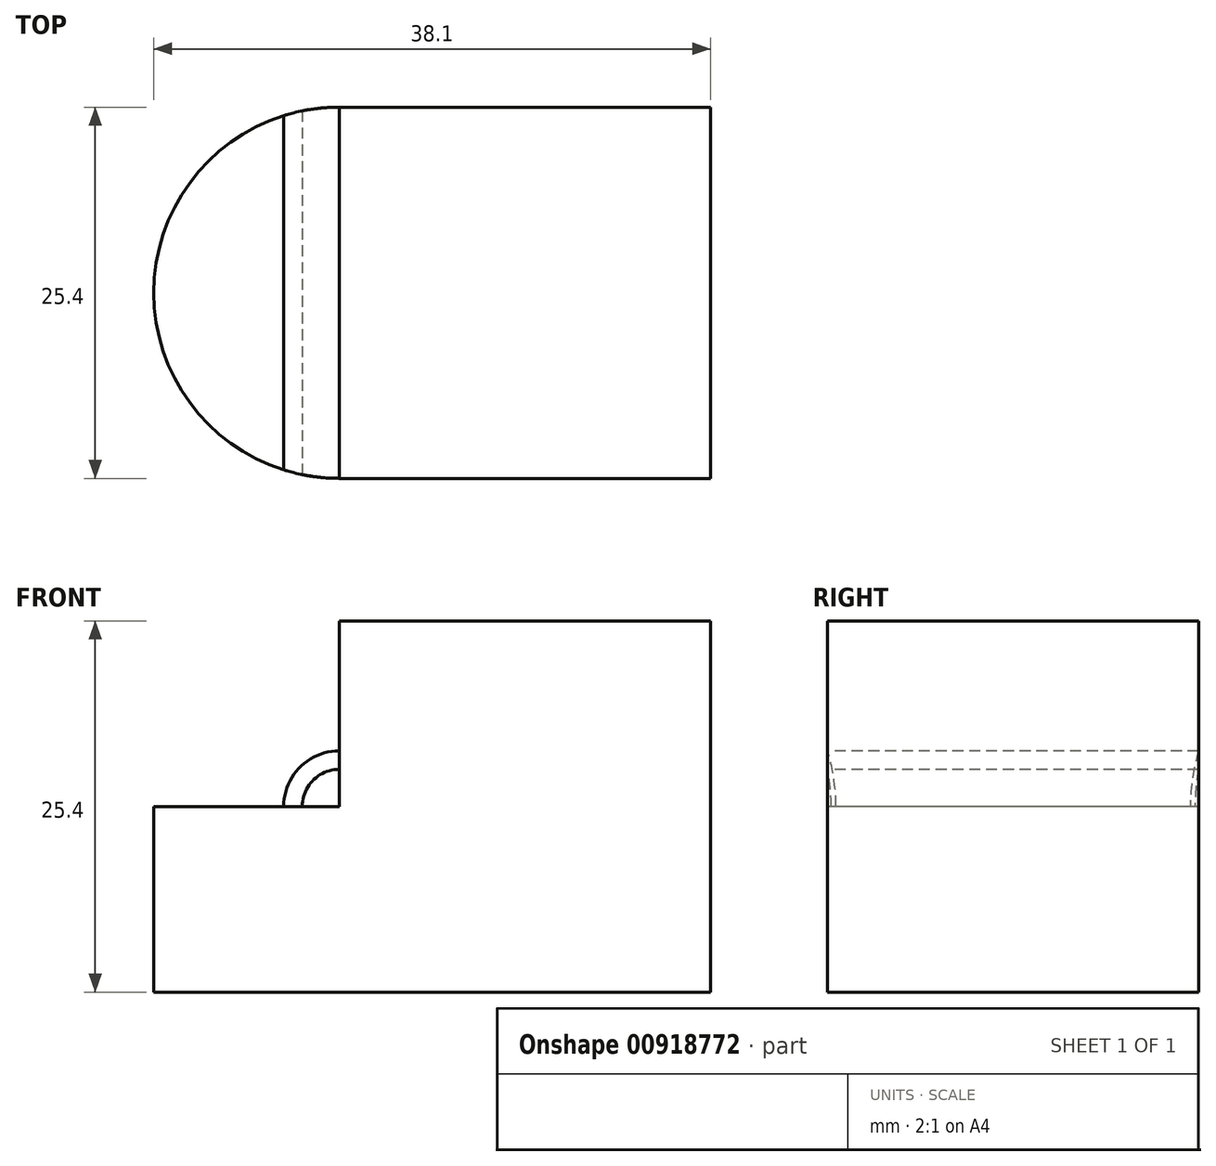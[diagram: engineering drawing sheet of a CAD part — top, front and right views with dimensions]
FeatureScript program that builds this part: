
annotation { "Feature Type Name" : "Feature", "Feature Type Description" : "" }
export const myFeature = defineFeature(function(context is Context, id is Id, definition is map)
    precondition{}
    {
        {
            var Q0;
            Q0=qCreatedBy(makeId("Top.planeOp"),FACE);
            var sketch = newSketch(context, id + "F0", { "sketchPlane" : qUnion([Q0])});
            skLineSegment(sketch, "E0", {"start": v(0, 0) * mm, "end": v(25.4, 0) * mm});
            skLineSegment(sketch, "E1", {"start": v(25.4, 0) * mm, "end": v(25.4, 25.4) * mm});
            skLineSegment(sketch, "E2", {"start": v(25.4, 25.4) * mm, "end": v(0, 25.4) * mm});
            skLineSegment(sketch, "E3", {"start": v(0, 25.4) * mm, "end": v(0, 0) * mm});
            skArc(sketch, "E4", {"start": v(0, 25.4) * mm, "mid": v(-12.7, 12.7) * mm, "end": v(0, 0) * mm});
            skSolve(sketch);
        }
        {
            var Q0;
            Q0=makeQuery(id+"F0.imprint","IMPRINT",FACE,{"disambiguationData":[TD([[makeQuery(id+"F0.imprint","IMPRINT",EDGE,{"derivedFrom":sQuery(id+"F0.wireOp",EDGE,"E3")}),-1.0]])]});
            extrude(context, id + "F1", {"entities" : qUnion([Q0]), "depth" : 12.7 * mm, "offsetDistance" : 25.4 * mm});
        }
        {
            var Q0;
            Q0=makeQuery(id+"F0.imprint","IMPRINT",FACE,{"disambiguationData":[TD([[makeQuery(id+"F0.imprint","IMPRINT",EDGE,{"derivedFrom":sQuery(id+"F0.wireOp",EDGE,"E0")}),1.0]])]});
            extrude(context, id + "F2", {"entities" : qUnion([Q0]), "operationType" : NewBodyOperationType.ADD, "depth" : 25.4 * mm, "offsetDistance" : 25.4 * mm});
        }
        {
            var Q0;
            Q0=makeQuery(id+"F2.opExtrude","SWEPT_FACE",FACE,{"disambiguationData":[OSD([sQuery(id+"F0.wireOp",EDGE,"E0")])]});
            var sketch = newSketch(context, id + "F3", { "sketchPlane" : qUnion([Q0])});
            skLineSegment(sketch, "E5", {"start": v(0, 12.7) * mm, "end": v(-2.54, 12.7) * mm});
            skLineSegment(sketch, "E6", {"start": v(0, 12.7) * mm, "end": v(0, 15.24) * mm});
            skArc(sketch, "E7", {"start": v(0, 15.24) * mm, "mid": v(-1.8, 14.5) * mm, "end": v(-2.54, 12.7) * mm});
            skSolve(sketch);
        }
        {
            var Q0;
            Q0=makeQuery(id+"F3.imprint","IMPRINT",FACE,{"disambiguationData":[TD([[makeQuery(id+"F3.imprint","IMPRINT",EDGE,{"derivedFrom":sQuery(id+"F3.wireOp",EDGE,"E5")}),-1.0]])]});
            extrude(context, id + "F4", {"entities" : qUnion([Q0]), "oppositeDirection" : true, "depth" : 25.4 * mm, "offsetDistance" : 25.4 * mm});
        }
        {
            var Q0;
            Q0=makeQuery(id+"F4.opExtrude","CAP_FACE",FACE,{"disambiguationData":[OSD([sQuery(id+"F3.wireOp",EDGE,"E5"),sQuery(id+"F3.wireOp",EDGE,"E6"),sQuery(id+"F3.wireOp",EDGE,"E7")])],"isStart":true});
            var sketch = newSketch(context, id + "F5", { "sketchPlane" : qUnion([Q0])});
            skLineSegment(sketch, "E8", {"start": v(-2.54, 12.7) * mm, "end": v(-3.81, 12.7) * mm});
            skLineSegment(sketch, "E9", {"start": v(0, 15.24) * mm, "end": v(0, 16.51) * mm});
            skArc(sketch, "E10", {"start": v(0, 15.24) * mm, "mid": v(-1.8, 14.5) * mm, "end": v(-2.54, 12.7) * mm});
            skArc(sketch, "E11", {"start": v(0, 16.51) * mm, "mid": v(-2.7, 15.4) * mm, "end": v(-3.81, 12.7) * mm});
            skSolve(sketch);
        }
        {
            var Q0;
            Q0 = qSketchRegion(id + "F5", true);
            extrude(context, id + "F6", {"entities" : qUnion([Q0]), "oppositeDirection" : true, "depth" : 25.4 * mm, "offsetDistance" : 25.4 * mm});
        }
        {
            var Q0;
            Q0=makeQuery(id+"F1.opExtrude","CAP_FACE",FACE,{"disambiguationData":[OSD([sQuery(id+"F0.wireOp",EDGE,"E3"),sQuery(id+"F0.wireOp",EDGE,"E4")])],"isStart":false});
            var sketch = newSketch(context, id + "F7", { "sketchPlane" : qUnion([Q0])});
            skArc(sketch, "E12", {"start": v(0, 25.4) * mm, "mid": v(-12.7, 12.7) * mm, "end": v(0, 0) * mm});
            skLineSegment(sketch, "E13", {"start": v(0, 25.4) * mm, "end": v(0, 0) * mm});
            skSolve(sketch);
        }
        {
            var Q0;
            Q0 = qSketchRegion(id + "F7", true);
            extrude(context, id + "F8", {"entities" : qUnion([Q0]), "depth" : 25.4 * mm, "offsetDistance" : 25.4 * mm});
        }
        {
            var Q0;
            Q0=makeQuery(id+"F8.opExtrude","SWEPT_BODY",BODY,{"disambiguationData":[OSD([sQuery(id+"F7.wireOp",EDGE,"E12"),sQuery(id+"F7.wireOp",EDGE,"E13")])]});
            var Q1;
            Q1=makeQuery(id+"F4.opExtrude","SWEPT_BODY",BODY,{"disambiguationData":[OSD([sQuery(id+"F3.wireOp",EDGE,"E5"),sQuery(id+"F3.wireOp",EDGE,"E6"),sQuery(id+"F3.wireOp",EDGE,"E7")])]});
            booleanBodies(context, id + "F9", {"operationType" : BooleanOperationType.INTERSECTION, "tools" : qUnion([Q0, Q1])});
        }
        {
            var Q0;
            Q0=makeQuery(id+"F1.opExtrude","CAP_FACE",FACE,{"disambiguationData":[OSD([sQuery(id+"F0.wireOp",EDGE,"E3"),sQuery(id+"F0.wireOp",EDGE,"E4")])],"isStart":false});
            extrude(context, id + "F10", {"entities" : qUnion([Q0]), "depth" : 25.4 * mm, "offsetDistance" : 25.4 * mm});
        }
        {
            var Q0;
            Q0=makeQuery(id+"F10.opExtrude","SWEPT_BODY",BODY,{"disambiguationData":[OSD([sQuery(id+"F0.wireOp",EDGE,"E3"),sQuery(id+"F0.wireOp",EDGE,"E4")])]});
            var Q1;
            Q1=makeQuery(id+"F6.opExtrude","SWEPT_BODY",BODY,{"disambiguationData":[OSD([sQuery(id+"F5.wireOp",EDGE,"E8"),sQuery(id+"F5.wireOp",EDGE,"E9"),sQuery(id+"F5.wireOp",EDGE,"E10"),sQuery(id+"F5.wireOp",EDGE,"E11")])]});
            booleanBodies(context, id + "F11", {"operationType" : BooleanOperationType.INTERSECTION, "tools" : qUnion([Q0, Q1])});
        }
    });
